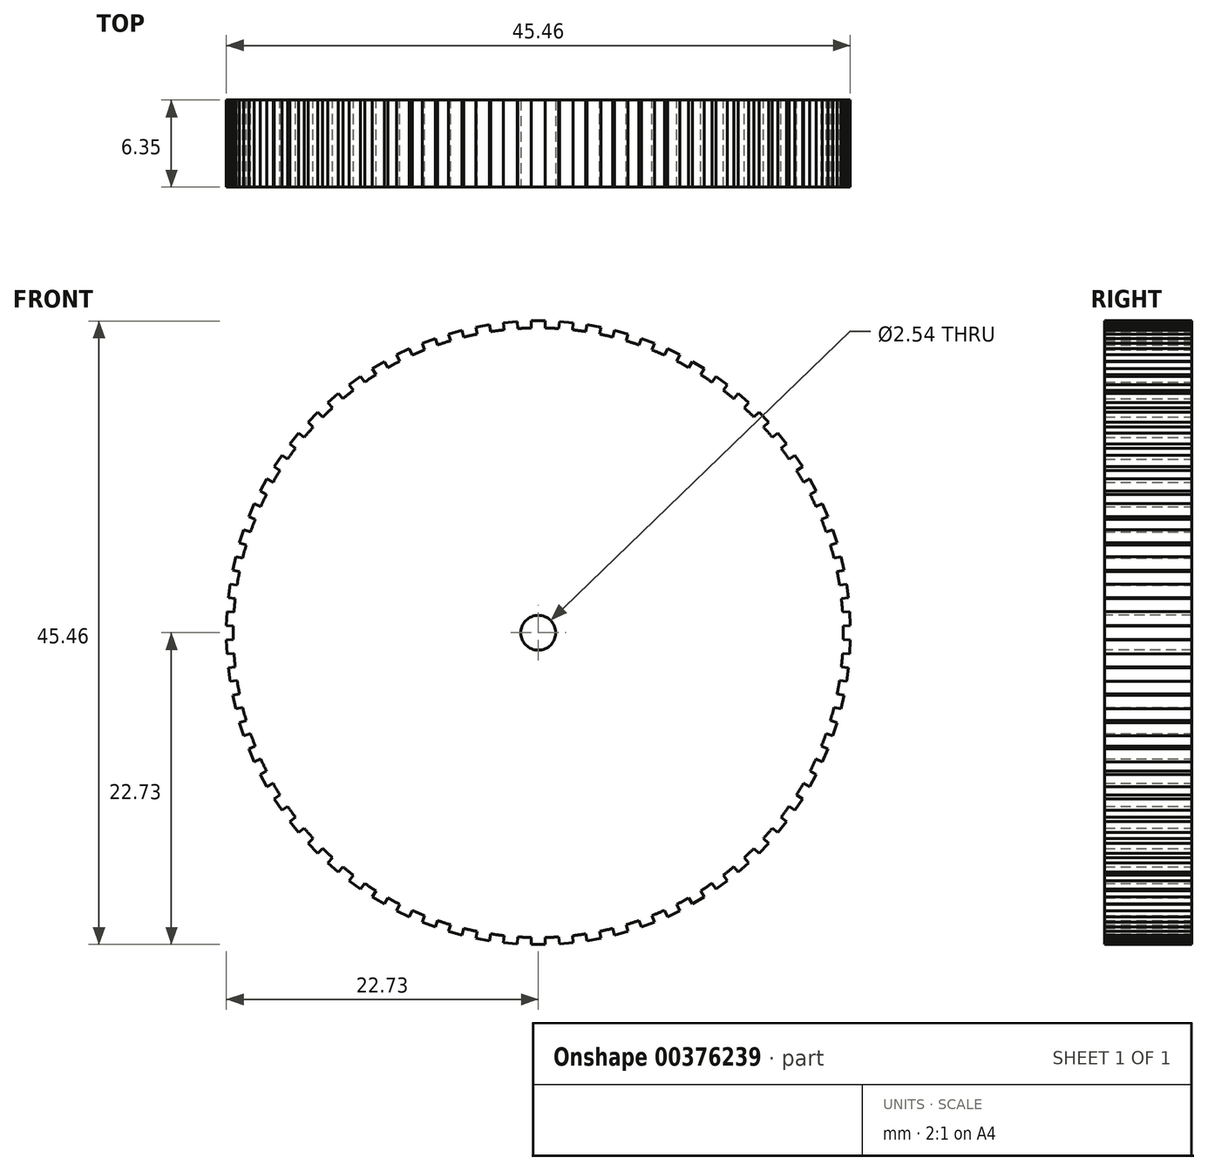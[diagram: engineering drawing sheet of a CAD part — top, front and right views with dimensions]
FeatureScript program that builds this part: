
annotation { "Feature Type Name" : "Feature", "Feature Type Description" : "" }
export const myFeature = defineFeature(function(context is Context, id is Id, definition is map)
    precondition{}
    {
        {
            var Q0;
            Q0=qCreatedBy(makeId("Front.planeOp"),FACE);
            var sketch = newSketch(context, id + "F0", { "sketchPlane" : qUnion([Q0])});
            skCircle(sketch, "E0", {"center": v(0, 0) * mm, "radius": 22.23 * mm});
            skLineSegment(sketch, "E1", {"start": v(0, 22.23) * mm, "end": v(0, 22.73) * mm});
            skLineSegment(sketch, "E2", {"start": v(0, 22.73) * mm, "end": v(0.5, 22.73) * mm});
            skLineSegment(sketch, "E3", {"start": v(0.5, 22.73) * mm, "end": v(0.5, 22.22) * mm});
            skLineSegment(sketch, "E4", {"start": v(0, 22.73) * mm, "end": v(-0.5, 22.73) * mm});
            skLineSegment(sketch, "E5", {"start": v(-0.5, 22.73) * mm, "end": v(-0.5, 22.22) * mm});
            skLineSegment(sketch, "E6.1.0", {"start": v(-1.53, 22.69) * mm, "end": v(-1.49, 22.18) * mm});
            skLineSegment(sketch, "E6.1.1", {"start": v(-2.04, 22.64) * mm, "end": v(-1.53, 22.69) * mm});
            skLineSegment(sketch, "E6.1.2", {"start": v(-2.04, 22.64) * mm, "end": v(-2.54, 22.6) * mm});
            skLineSegment(sketch, "E6.1.3", {"start": v(-2.54, 22.6) * mm, "end": v(-2.5, 22.08) * mm});
            skLineSegment(sketch, "E6.2.0", {"start": v(-3.56, 22.46) * mm, "end": v(-3.47, 21.95) * mm});
            skLineSegment(sketch, "E6.2.1", {"start": v(-4.06, 22.37) * mm, "end": v(-3.56, 22.46) * mm});
            skLineSegment(sketch, "E6.2.2", {"start": v(-4.06, 22.37) * mm, "end": v(-4.56, 22.28) * mm});
            skLineSegment(sketch, "E6.2.3", {"start": v(-4.56, 22.28) * mm, "end": v(-4.47, 21.77) * mm});
            skLineSegment(sketch, "E6.3.0", {"start": v(-5.56, 22.05) * mm, "end": v(-5.42, 21.55) * mm});
            skLineSegment(sketch, "E6.3.1", {"start": v(-6.05, 21.91) * mm, "end": v(-5.56, 22.05) * mm});
            skLineSegment(sketch, "E6.3.2", {"start": v(-6.05, 21.91) * mm, "end": v(-6.54, 21.78) * mm});
            skLineSegment(sketch, "E6.3.3", {"start": v(-6.54, 21.78) * mm, "end": v(-6.4, 21.28) * mm});
            skLineSegment(sketch, "E6.4.0", {"start": v(-7.51, 21.46) * mm, "end": v(-7.33, 20.98) * mm});
            skLineSegment(sketch, "E6.4.1", {"start": v(-7.99, 21.28) * mm, "end": v(-7.51, 21.46) * mm});
            skLineSegment(sketch, "E6.4.2", {"start": v(-7.99, 21.28) * mm, "end": v(-8.46, 21.1) * mm});
            skLineSegment(sketch, "E6.4.3", {"start": v(-8.46, 21.1) * mm, "end": v(-8.28, 20.62) * mm});
            skLineSegment(sketch, "E6.5.0", {"start": v(-9.4, 20.7) * mm, "end": v(-9.18, 20.24) * mm});
            skLineSegment(sketch, "E6.5.1", {"start": v(-9.86, 20.48) * mm, "end": v(-9.4, 20.7) * mm});
            skLineSegment(sketch, "E6.5.2", {"start": v(-9.86, 20.48) * mm, "end": v(-10.32, 20.26) * mm});
            skLineSegment(sketch, "E6.5.3", {"start": v(-10.32, 20.26) * mm, "end": v(-10.1, 19.8) * mm});
            skLineSegment(sketch, "E6.6.0", {"start": v(-11.22, 19.78) * mm, "end": v(-10.96, 19.33) * mm});
            skLineSegment(sketch, "E6.6.1", {"start": v(-11.66, 19.52) * mm, "end": v(-11.22, 19.78) * mm});
            skLineSegment(sketch, "E6.6.2", {"start": v(-11.66, 19.52) * mm, "end": v(-12.1, 19.25) * mm});
            skLineSegment(sketch, "E6.6.3", {"start": v(-12.1, 19.25) * mm, "end": v(-11.83, 18.81) * mm});
            skLineSegment(sketch, "E6.7.0", {"start": v(-12.95, 18.69) * mm, "end": v(-12.65, 18.27) * mm});
            skLineSegment(sketch, "E6.7.1", {"start": v(-13.36, 18.4) * mm, "end": v(-12.95, 18.69) * mm});
            skLineSegment(sketch, "E6.7.2", {"start": v(-13.36, 18.4) * mm, "end": v(-13.77, 18.1) * mm});
            skLineSegment(sketch, "E6.7.3", {"start": v(-13.77, 18.1) * mm, "end": v(-13.47, 17.68) * mm});
            skLineSegment(sketch, "E6.8.0", {"start": v(-14.57, 17.45) * mm, "end": v(-14.24, 17.07) * mm});
            skLineSegment(sketch, "E6.8.1", {"start": v(-14.96, 17.12) * mm, "end": v(-14.57, 17.45) * mm});
            skLineSegment(sketch, "E6.8.2", {"start": v(-14.96, 17.12) * mm, "end": v(-15.34, 16.79) * mm});
            skLineSegment(sketch, "E6.8.3", {"start": v(-15.34, 16.79) * mm, "end": v(-15, 16.4) * mm});
            skLineSegment(sketch, "E6.9.0", {"start": v(-16.08, 16.08) * mm, "end": v(-15.7, 15.72) * mm});
            skLineSegment(sketch, "E6.9.1", {"start": v(-16.43, 15.7) * mm, "end": v(-16.08, 16.08) * mm});
            skLineSegment(sketch, "E6.9.2", {"start": v(-16.43, 15.7) * mm, "end": v(-16.78, 15.34) * mm});
            skLineSegment(sketch, "E6.9.3", {"start": v(-16.78, 15.34) * mm, "end": v(-16.41, 14.99) * mm});
            skLineSegment(sketch, "E6.10.0", {"start": v(-17.46, 14.57) * mm, "end": v(-17.05, 14.25) * mm});
            skLineSegment(sketch, "E6.10.1", {"start": v(-17.77, 14.17) * mm, "end": v(-17.46, 14.57) * mm});
            skLineSegment(sketch, "E6.10.2", {"start": v(-17.77, 14.17) * mm, "end": v(-18.1, 13.78) * mm});
            skLineSegment(sketch, "E6.10.3", {"start": v(-18.1, 13.78) * mm, "end": v(-17.69, 13.46) * mm});
            skLineSegment(sketch, "E6.11.0", {"start": v(-18.7, 12.95) * mm, "end": v(-18.26, 12.66) * mm});
            skLineSegment(sketch, "E6.11.1", {"start": v(-18.97, 12.52) * mm, "end": v(-18.7, 12.95) * mm});
            skLineSegment(sketch, "E6.11.2", {"start": v(-18.97, 12.52) * mm, "end": v(-19.25, 12.1) * mm});
            skLineSegment(sketch, "E6.11.3", {"start": v(-19.25, 12.1) * mm, "end": v(-18.82, 11.82) * mm});
            skLineSegment(sketch, "E6.12.0", {"start": v(-19.78, 11.22) * mm, "end": v(-19.33, 10.98) * mm});
            skLineSegment(sketch, "E6.12.1", {"start": v(-20.02, 10.77) * mm, "end": v(-19.78, 11.22) * mm});
            skLineSegment(sketch, "E6.12.2", {"start": v(-20.02, 10.77) * mm, "end": v(-20.26, 10.33) * mm});
            skLineSegment(sketch, "E6.12.3", {"start": v(-20.26, 10.33) * mm, "end": v(-19.8, 10.08) * mm});
            skLineSegment(sketch, "E6.13.0", {"start": v(-20.7, 9.4) * mm, "end": v(-20.23, 9.2) * mm});
            skLineSegment(sketch, "E6.13.1", {"start": v(-20.9, 8.93) * mm, "end": v(-20.7, 9.4) * mm});
            skLineSegment(sketch, "E6.13.2", {"start": v(-20.9, 8.93) * mm, "end": v(-21.1, 8.47) * mm});
            skLineSegment(sketch, "E6.13.3", {"start": v(-21.1, 8.47) * mm, "end": v(-20.63, 8.27) * mm});
            skLineSegment(sketch, "E6.14.0", {"start": v(-21.46, 7.5) * mm, "end": v(-20.97, 7.35) * mm});
            skLineSegment(sketch, "E6.14.1", {"start": v(-21.62, 7.02) * mm, "end": v(-21.46, 7.5) * mm});
            skLineSegment(sketch, "E6.14.2", {"start": v(-21.62, 7.02) * mm, "end": v(-21.78, 6.54) * mm});
            skLineSegment(sketch, "E6.14.3", {"start": v(-21.78, 6.54) * mm, "end": v(-21.29, 6.38) * mm});
            skLineSegment(sketch, "E6.15.0", {"start": v(-22.05, 5.55) * mm, "end": v(-21.55, 5.44) * mm});
            skLineSegment(sketch, "E6.15.1", {"start": v(-22.16, 5.06) * mm, "end": v(-22.05, 5.55) * mm});
            skLineSegment(sketch, "E6.15.2", {"start": v(-22.16, 5.06) * mm, "end": v(-22.28, 4.56) * mm});
            skLineSegment(sketch, "E6.15.3", {"start": v(-22.28, 4.56) * mm, "end": v(-21.78, 4.45) * mm});
            skLineSegment(sketch, "E6.16.0", {"start": v(-22.46, 3.55) * mm, "end": v(-21.95, 3.49) * mm});
            skLineSegment(sketch, "E6.16.1", {"start": v(-22.53, 3.05) * mm, "end": v(-22.46, 3.55) * mm});
            skLineSegment(sketch, "E6.16.2", {"start": v(-22.53, 3.05) * mm, "end": v(-22.6, 2.55) * mm});
            skLineSegment(sketch, "E6.16.3", {"start": v(-22.6, 2.55) * mm, "end": v(-22.09, 2.48) * mm});
            skLineSegment(sketch, "E6.17.0", {"start": v(-22.69, 1.53) * mm, "end": v(-22.17, 1.5) * mm});
            skLineSegment(sketch, "E6.17.1", {"start": v(-22.71, 1.02) * mm, "end": v(-22.69, 1.53) * mm});
            skLineSegment(sketch, "E6.17.2", {"start": v(-22.71, 1.02) * mm, "end": v(-22.73, 0.51) * mm});
            skLineSegment(sketch, "E6.17.3", {"start": v(-22.73, 0.51) * mm, "end": v(-22.22, 0.49) * mm});
            skLineSegment(sketch, "E6.18.0", {"start": v(-22.73, -0.51) * mm, "end": v(-22.22, -0.49) * mm});
            skLineSegment(sketch, "E6.18.1", {"start": v(-22.71, -1.02) * mm, "end": v(-22.73, -0.51) * mm});
            skLineSegment(sketch, "E6.18.2", {"start": v(-22.71, -1.02) * mm, "end": v(-22.69, -1.53) * mm});
            skLineSegment(sketch, "E6.18.3", {"start": v(-22.69, -1.53) * mm, "end": v(-22.17, -1.5) * mm});
            skLineSegment(sketch, "E6.19.0", {"start": v(-22.6, -2.55) * mm, "end": v(-22.09, -2.48) * mm});
            skLineSegment(sketch, "E6.19.1", {"start": v(-22.53, -3.05) * mm, "end": v(-22.6, -2.55) * mm});
            skLineSegment(sketch, "E6.19.2", {"start": v(-22.53, -3.05) * mm, "end": v(-22.46, -3.55) * mm});
            skLineSegment(sketch, "E6.19.3", {"start": v(-22.46, -3.55) * mm, "end": v(-21.95, -3.49) * mm});
            skLineSegment(sketch, "E6.20.0", {"start": v(-22.28, -4.56) * mm, "end": v(-21.78, -4.45) * mm});
            skLineSegment(sketch, "E6.20.1", {"start": v(-22.16, -5.06) * mm, "end": v(-22.28, -4.56) * mm});
            skLineSegment(sketch, "E6.20.2", {"start": v(-22.16, -5.06) * mm, "end": v(-22.05, -5.55) * mm});
            skLineSegment(sketch, "E6.20.3", {"start": v(-22.05, -5.55) * mm, "end": v(-21.55, -5.44) * mm});
            skLineSegment(sketch, "E6.21.0", {"start": v(-21.78, -6.54) * mm, "end": v(-21.29, -6.38) * mm});
            skLineSegment(sketch, "E6.21.1", {"start": v(-21.62, -7.02) * mm, "end": v(-21.78, -6.54) * mm});
            skLineSegment(sketch, "E6.21.2", {"start": v(-21.62, -7.02) * mm, "end": v(-21.46, -7.5) * mm});
            skLineSegment(sketch, "E6.21.3", {"start": v(-21.46, -7.5) * mm, "end": v(-20.97, -7.35) * mm});
            skLineSegment(sketch, "E6.22.0", {"start": v(-21.1, -8.47) * mm, "end": v(-20.63, -8.27) * mm});
            skLineSegment(sketch, "E6.22.1", {"start": v(-20.9, -8.93) * mm, "end": v(-21.1, -8.47) * mm});
            skLineSegment(sketch, "E6.22.2", {"start": v(-20.9, -8.93) * mm, "end": v(-20.7, -9.4) * mm});
            skLineSegment(sketch, "E6.22.3", {"start": v(-20.7, -9.4) * mm, "end": v(-20.23, -9.2) * mm});
            skLineSegment(sketch, "E6.23.0", {"start": v(-20.26, -10.33) * mm, "end": v(-19.8, -10.08) * mm});
            skLineSegment(sketch, "E6.23.1", {"start": v(-20.02, -10.77) * mm, "end": v(-20.26, -10.33) * mm});
            skLineSegment(sketch, "E6.23.2", {"start": v(-20.02, -10.77) * mm, "end": v(-19.78, -11.22) * mm});
            skLineSegment(sketch, "E6.23.3", {"start": v(-19.78, -11.22) * mm, "end": v(-19.33, -10.98) * mm});
            skLineSegment(sketch, "E6.24.0", {"start": v(-19.25, -12.1) * mm, "end": v(-18.82, -11.82) * mm});
            skLineSegment(sketch, "E6.24.1", {"start": v(-18.97, -12.52) * mm, "end": v(-19.25, -12.1) * mm});
            skLineSegment(sketch, "E6.24.2", {"start": v(-18.97, -12.52) * mm, "end": v(-18.7, -12.95) * mm});
            skLineSegment(sketch, "E6.24.3", {"start": v(-18.7, -12.95) * mm, "end": v(-18.26, -12.66) * mm});
            skLineSegment(sketch, "E6.25.0", {"start": v(-18.1, -13.78) * mm, "end": v(-17.69, -13.46) * mm});
            skLineSegment(sketch, "E6.25.1", {"start": v(-17.77, -14.17) * mm, "end": v(-18.1, -13.78) * mm});
            skLineSegment(sketch, "E6.25.2", {"start": v(-17.77, -14.17) * mm, "end": v(-17.46, -14.57) * mm});
            skLineSegment(sketch, "E6.25.3", {"start": v(-17.46, -14.57) * mm, "end": v(-17.05, -14.25) * mm});
            skLineSegment(sketch, "E6.26.0", {"start": v(-16.78, -15.34) * mm, "end": v(-16.41, -14.99) * mm});
            skLineSegment(sketch, "E6.26.1", {"start": v(-16.43, -15.7) * mm, "end": v(-16.78, -15.34) * mm});
            skLineSegment(sketch, "E6.26.2", {"start": v(-16.43, -15.7) * mm, "end": v(-16.08, -16.08) * mm});
            skLineSegment(sketch, "E6.26.3", {"start": v(-16.08, -16.08) * mm, "end": v(-15.7, -15.72) * mm});
            skLineSegment(sketch, "E6.27.0", {"start": v(-15.34, -16.79) * mm, "end": v(-15, -16.4) * mm});
            skLineSegment(sketch, "E6.27.1", {"start": v(-14.96, -17.12) * mm, "end": v(-15.34, -16.79) * mm});
            skLineSegment(sketch, "E6.27.2", {"start": v(-14.96, -17.12) * mm, "end": v(-14.57, -17.45) * mm});
            skLineSegment(sketch, "E6.27.3", {"start": v(-14.57, -17.45) * mm, "end": v(-14.24, -17.07) * mm});
            skLineSegment(sketch, "E6.28.0", {"start": v(-13.77, -18.1) * mm, "end": v(-13.47, -17.68) * mm});
            skLineSegment(sketch, "E6.28.1", {"start": v(-13.36, -18.4) * mm, "end": v(-13.77, -18.1) * mm});
            skLineSegment(sketch, "E6.28.2", {"start": v(-13.36, -18.4) * mm, "end": v(-12.95, -18.69) * mm});
            skLineSegment(sketch, "E6.28.3", {"start": v(-12.95, -18.69) * mm, "end": v(-12.65, -18.27) * mm});
            skLineSegment(sketch, "E6.29.0", {"start": v(-12.1, -19.25) * mm, "end": v(-11.83, -18.81) * mm});
            skLineSegment(sketch, "E6.29.1", {"start": v(-11.66, -19.52) * mm, "end": v(-12.1, -19.25) * mm});
            skLineSegment(sketch, "E6.29.2", {"start": v(-11.66, -19.52) * mm, "end": v(-11.22, -19.78) * mm});
            skLineSegment(sketch, "E6.29.3", {"start": v(-11.22, -19.78) * mm, "end": v(-10.96, -19.33) * mm});
            skLineSegment(sketch, "E6.30.0", {"start": v(-10.32, -20.26) * mm, "end": v(-10.1, -19.8) * mm});
            skLineSegment(sketch, "E6.30.1", {"start": v(-9.86, -20.48) * mm, "end": v(-10.32, -20.26) * mm});
            skLineSegment(sketch, "E6.30.2", {"start": v(-9.86, -20.48) * mm, "end": v(-9.4, -20.7) * mm});
            skLineSegment(sketch, "E6.30.3", {"start": v(-9.4, -20.7) * mm, "end": v(-9.18, -20.24) * mm});
            skLineSegment(sketch, "E6.31.0", {"start": v(-8.46, -21.1) * mm, "end": v(-8.28, -20.62) * mm});
            skLineSegment(sketch, "E6.31.1", {"start": v(-7.99, -21.28) * mm, "end": v(-8.46, -21.1) * mm});
            skLineSegment(sketch, "E6.31.2", {"start": v(-7.99, -21.28) * mm, "end": v(-7.51, -21.46) * mm});
            skLineSegment(sketch, "E6.31.3", {"start": v(-7.51, -21.46) * mm, "end": v(-7.33, -20.98) * mm});
            skLineSegment(sketch, "E6.32.0", {"start": v(-6.54, -21.78) * mm, "end": v(-6.4, -21.28) * mm});
            skLineSegment(sketch, "E6.32.1", {"start": v(-6.05, -21.91) * mm, "end": v(-6.54, -21.78) * mm});
            skLineSegment(sketch, "E6.32.2", {"start": v(-6.05, -21.91) * mm, "end": v(-5.56, -22.05) * mm});
            skLineSegment(sketch, "E6.32.3", {"start": v(-5.56, -22.05) * mm, "end": v(-5.42, -21.55) * mm});
            skLineSegment(sketch, "E6.33.0", {"start": v(-4.56, -22.28) * mm, "end": v(-4.47, -21.77) * mm});
            skLineSegment(sketch, "E6.33.1", {"start": v(-4.06, -22.37) * mm, "end": v(-4.56, -22.28) * mm});
            skLineSegment(sketch, "E6.33.2", {"start": v(-4.06, -22.37) * mm, "end": v(-3.56, -22.46) * mm});
            skLineSegment(sketch, "E6.33.3", {"start": v(-3.56, -22.46) * mm, "end": v(-3.47, -21.95) * mm});
            skLineSegment(sketch, "E6.34.0", {"start": v(-2.54, -22.6) * mm, "end": v(-2.5, -22.08) * mm});
            skLineSegment(sketch, "E6.34.1", {"start": v(-2.04, -22.64) * mm, "end": v(-2.54, -22.6) * mm});
            skLineSegment(sketch, "E6.34.2", {"start": v(-2.04, -22.64) * mm, "end": v(-1.53, -22.69) * mm});
            skLineSegment(sketch, "E6.34.3", {"start": v(-1.53, -22.69) * mm, "end": v(-1.49, -22.18) * mm});
            skLineSegment(sketch, "E6.35.0", {"start": v(-0.5, -22.73) * mm, "end": v(-0.5, -22.22) * mm});
            skLineSegment(sketch, "E6.35.1", {"start": v(0, -22.73) * mm, "end": v(-0.5, -22.73) * mm});
            skLineSegment(sketch, "E6.35.2", {"start": v(0, -22.73) * mm, "end": v(0.5, -22.73) * mm});
            skLineSegment(sketch, "E6.35.3", {"start": v(0.5, -22.73) * mm, "end": v(0.5, -22.22) * mm});
            skLineSegment(sketch, "E6.36.0", {"start": v(1.53, -22.69) * mm, "end": v(1.49, -22.18) * mm});
            skLineSegment(sketch, "E6.36.1", {"start": v(2.04, -22.64) * mm, "end": v(1.53, -22.69) * mm});
            skLineSegment(sketch, "E6.36.2", {"start": v(2.04, -22.64) * mm, "end": v(2.54, -22.6) * mm});
            skLineSegment(sketch, "E6.36.3", {"start": v(2.54, -22.6) * mm, "end": v(2.5, -22.08) * mm});
            skLineSegment(sketch, "E6.37.0", {"start": v(3.56, -22.46) * mm, "end": v(3.47, -21.95) * mm});
            skLineSegment(sketch, "E6.37.1", {"start": v(4.06, -22.37) * mm, "end": v(3.56, -22.46) * mm});
            skLineSegment(sketch, "E6.37.2", {"start": v(4.06, -22.37) * mm, "end": v(4.56, -22.28) * mm});
            skLineSegment(sketch, "E6.37.3", {"start": v(4.56, -22.28) * mm, "end": v(4.47, -21.77) * mm});
            skLineSegment(sketch, "E6.38.0", {"start": v(5.56, -22.05) * mm, "end": v(5.42, -21.55) * mm});
            skLineSegment(sketch, "E6.38.1", {"start": v(6.05, -21.91) * mm, "end": v(5.56, -22.05) * mm});
            skLineSegment(sketch, "E6.38.2", {"start": v(6.05, -21.91) * mm, "end": v(6.54, -21.78) * mm});
            skLineSegment(sketch, "E6.38.3", {"start": v(6.54, -21.78) * mm, "end": v(6.4, -21.28) * mm});
            skLineSegment(sketch, "E6.39.0", {"start": v(7.51, -21.46) * mm, "end": v(7.33, -20.98) * mm});
            skLineSegment(sketch, "E6.39.1", {"start": v(7.99, -21.28) * mm, "end": v(7.51, -21.46) * mm});
            skLineSegment(sketch, "E6.39.2", {"start": v(7.99, -21.28) * mm, "end": v(8.46, -21.1) * mm});
            skLineSegment(sketch, "E6.39.3", {"start": v(8.46, -21.1) * mm, "end": v(8.28, -20.62) * mm});
            skLineSegment(sketch, "E6.40.0", {"start": v(9.4, -20.7) * mm, "end": v(9.18, -20.24) * mm});
            skLineSegment(sketch, "E6.40.1", {"start": v(9.86, -20.48) * mm, "end": v(9.4, -20.7) * mm});
            skLineSegment(sketch, "E6.40.2", {"start": v(9.86, -20.48) * mm, "end": v(10.32, -20.26) * mm});
            skLineSegment(sketch, "E6.40.3", {"start": v(10.32, -20.26) * mm, "end": v(10.1, -19.8) * mm});
            skLineSegment(sketch, "E6.41.0", {"start": v(11.22, -19.78) * mm, "end": v(10.96, -19.33) * mm});
            skLineSegment(sketch, "E6.41.1", {"start": v(11.66, -19.52) * mm, "end": v(11.22, -19.78) * mm});
            skLineSegment(sketch, "E6.41.2", {"start": v(11.66, -19.52) * mm, "end": v(12.1, -19.25) * mm});
            skLineSegment(sketch, "E6.41.3", {"start": v(12.1, -19.25) * mm, "end": v(11.83, -18.81) * mm});
            skLineSegment(sketch, "E6.42.0", {"start": v(12.95, -18.69) * mm, "end": v(12.65, -18.27) * mm});
            skLineSegment(sketch, "E6.42.1", {"start": v(13.36, -18.4) * mm, "end": v(12.95, -18.69) * mm});
            skLineSegment(sketch, "E6.42.2", {"start": v(13.36, -18.4) * mm, "end": v(13.77, -18.1) * mm});
            skLineSegment(sketch, "E6.42.3", {"start": v(13.77, -18.1) * mm, "end": v(13.47, -17.68) * mm});
            skLineSegment(sketch, "E6.43.0", {"start": v(14.57, -17.45) * mm, "end": v(14.24, -17.07) * mm});
            skLineSegment(sketch, "E6.43.1", {"start": v(14.96, -17.12) * mm, "end": v(14.57, -17.45) * mm});
            skLineSegment(sketch, "E6.43.2", {"start": v(14.96, -17.12) * mm, "end": v(15.34, -16.79) * mm});
            skLineSegment(sketch, "E6.43.3", {"start": v(15.34, -16.79) * mm, "end": v(15, -16.4) * mm});
            skLineSegment(sketch, "E6.44.0", {"start": v(16.08, -16.08) * mm, "end": v(15.7, -15.72) * mm});
            skLineSegment(sketch, "E6.44.1", {"start": v(16.43, -15.7) * mm, "end": v(16.08, -16.08) * mm});
            skLineSegment(sketch, "E6.44.2", {"start": v(16.43, -15.7) * mm, "end": v(16.78, -15.34) * mm});
            skLineSegment(sketch, "E6.44.3", {"start": v(16.78, -15.34) * mm, "end": v(16.41, -14.99) * mm});
            skLineSegment(sketch, "E6.45.0", {"start": v(17.46, -14.57) * mm, "end": v(17.05, -14.25) * mm});
            skLineSegment(sketch, "E6.45.1", {"start": v(17.77, -14.17) * mm, "end": v(17.46, -14.57) * mm});
            skLineSegment(sketch, "E6.45.2", {"start": v(17.77, -14.17) * mm, "end": v(18.1, -13.78) * mm});
            skLineSegment(sketch, "E6.45.3", {"start": v(18.1, -13.78) * mm, "end": v(17.69, -13.46) * mm});
            skLineSegment(sketch, "E6.46.0", {"start": v(18.7, -12.95) * mm, "end": v(18.26, -12.66) * mm});
            skLineSegment(sketch, "E6.46.1", {"start": v(18.97, -12.52) * mm, "end": v(18.7, -12.95) * mm});
            skLineSegment(sketch, "E6.46.2", {"start": v(18.97, -12.52) * mm, "end": v(19.25, -12.1) * mm});
            skLineSegment(sketch, "E6.46.3", {"start": v(19.25, -12.1) * mm, "end": v(18.82, -11.82) * mm});
            skLineSegment(sketch, "E6.47.0", {"start": v(19.78, -11.22) * mm, "end": v(19.33, -10.98) * mm});
            skLineSegment(sketch, "E6.47.1", {"start": v(20.02, -10.77) * mm, "end": v(19.78, -11.22) * mm});
            skLineSegment(sketch, "E6.47.2", {"start": v(20.02, -10.77) * mm, "end": v(20.26, -10.33) * mm});
            skLineSegment(sketch, "E6.47.3", {"start": v(20.26, -10.33) * mm, "end": v(19.8, -10.08) * mm});
            skLineSegment(sketch, "E6.48.0", {"start": v(20.7, -9.4) * mm, "end": v(20.23, -9.2) * mm});
            skLineSegment(sketch, "E6.48.1", {"start": v(20.9, -8.93) * mm, "end": v(20.7, -9.4) * mm});
            skLineSegment(sketch, "E6.48.2", {"start": v(20.9, -8.93) * mm, "end": v(21.1, -8.47) * mm});
            skLineSegment(sketch, "E6.48.3", {"start": v(21.1, -8.47) * mm, "end": v(20.63, -8.27) * mm});
            skLineSegment(sketch, "E6.49.0", {"start": v(21.46, -7.5) * mm, "end": v(20.97, -7.35) * mm});
            skLineSegment(sketch, "E6.49.1", {"start": v(21.62, -7.02) * mm, "end": v(21.46, -7.5) * mm});
            skLineSegment(sketch, "E6.49.2", {"start": v(21.62, -7.02) * mm, "end": v(21.78, -6.54) * mm});
            skLineSegment(sketch, "E6.49.3", {"start": v(21.78, -6.54) * mm, "end": v(21.29, -6.38) * mm});
            skLineSegment(sketch, "E6.50.0", {"start": v(22.05, -5.55) * mm, "end": v(21.55, -5.44) * mm});
            skLineSegment(sketch, "E6.50.1", {"start": v(22.16, -5.06) * mm, "end": v(22.05, -5.55) * mm});
            skLineSegment(sketch, "E6.50.2", {"start": v(22.16, -5.06) * mm, "end": v(22.28, -4.56) * mm});
            skLineSegment(sketch, "E6.50.3", {"start": v(22.28, -4.56) * mm, "end": v(21.78, -4.45) * mm});
            skLineSegment(sketch, "E6.51.0", {"start": v(22.46, -3.55) * mm, "end": v(21.95, -3.49) * mm});
            skLineSegment(sketch, "E6.51.1", {"start": v(22.53, -3.05) * mm, "end": v(22.46, -3.55) * mm});
            skLineSegment(sketch, "E6.51.2", {"start": v(22.53, -3.05) * mm, "end": v(22.6, -2.55) * mm});
            skLineSegment(sketch, "E6.51.3", {"start": v(22.6, -2.55) * mm, "end": v(22.09, -2.48) * mm});
            skLineSegment(sketch, "E6.52.0", {"start": v(22.69, -1.53) * mm, "end": v(22.17, -1.5) * mm});
            skLineSegment(sketch, "E6.52.1", {"start": v(22.71, -1.02) * mm, "end": v(22.69, -1.53) * mm});
            skLineSegment(sketch, "E6.52.2", {"start": v(22.71, -1.02) * mm, "end": v(22.73, -0.51) * mm});
            skLineSegment(sketch, "E6.52.3", {"start": v(22.73, -0.51) * mm, "end": v(22.22, -0.49) * mm});
            skLineSegment(sketch, "E6.53.0", {"start": v(22.73, 0.51) * mm, "end": v(22.22, 0.49) * mm});
            skLineSegment(sketch, "E6.53.1", {"start": v(22.71, 1.02) * mm, "end": v(22.73, 0.51) * mm});
            skLineSegment(sketch, "E6.53.2", {"start": v(22.71, 1.02) * mm, "end": v(22.69, 1.53) * mm});
            skLineSegment(sketch, "E6.53.3", {"start": v(22.69, 1.53) * mm, "end": v(22.17, 1.5) * mm});
            skLineSegment(sketch, "E6.54.0", {"start": v(22.6, 2.55) * mm, "end": v(22.09, 2.48) * mm});
            skLineSegment(sketch, "E6.54.1", {"start": v(22.53, 3.05) * mm, "end": v(22.6, 2.55) * mm});
            skLineSegment(sketch, "E6.54.2", {"start": v(22.53, 3.05) * mm, "end": v(22.46, 3.55) * mm});
            skLineSegment(sketch, "E6.54.3", {"start": v(22.46, 3.55) * mm, "end": v(21.95, 3.49) * mm});
            skLineSegment(sketch, "E6.55.0", {"start": v(22.28, 4.56) * mm, "end": v(21.78, 4.45) * mm});
            skLineSegment(sketch, "E6.55.1", {"start": v(22.16, 5.06) * mm, "end": v(22.28, 4.56) * mm});
            skLineSegment(sketch, "E6.55.2", {"start": v(22.16, 5.06) * mm, "end": v(22.05, 5.55) * mm});
            skLineSegment(sketch, "E6.55.3", {"start": v(22.05, 5.55) * mm, "end": v(21.55, 5.44) * mm});
            skLineSegment(sketch, "E6.56.0", {"start": v(21.78, 6.54) * mm, "end": v(21.29, 6.38) * mm});
            skLineSegment(sketch, "E6.56.1", {"start": v(21.62, 7.02) * mm, "end": v(21.78, 6.54) * mm});
            skLineSegment(sketch, "E6.56.2", {"start": v(21.62, 7.02) * mm, "end": v(21.46, 7.5) * mm});
            skLineSegment(sketch, "E6.56.3", {"start": v(21.46, 7.5) * mm, "end": v(20.97, 7.35) * mm});
            skLineSegment(sketch, "E6.57.0", {"start": v(21.1, 8.47) * mm, "end": v(20.63, 8.27) * mm});
            skLineSegment(sketch, "E6.57.1", {"start": v(20.9, 8.93) * mm, "end": v(21.1, 8.47) * mm});
            skLineSegment(sketch, "E6.57.2", {"start": v(20.9, 8.93) * mm, "end": v(20.7, 9.4) * mm});
            skLineSegment(sketch, "E6.57.3", {"start": v(20.7, 9.4) * mm, "end": v(20.23, 9.2) * mm});
            skLineSegment(sketch, "E6.58.0", {"start": v(20.26, 10.33) * mm, "end": v(19.8, 10.08) * mm});
            skLineSegment(sketch, "E6.58.1", {"start": v(20.02, 10.77) * mm, "end": v(20.26, 10.33) * mm});
            skLineSegment(sketch, "E6.58.2", {"start": v(20.02, 10.77) * mm, "end": v(19.78, 11.22) * mm});
            skLineSegment(sketch, "E6.58.3", {"start": v(19.78, 11.22) * mm, "end": v(19.33, 10.98) * mm});
            skLineSegment(sketch, "E6.59.0", {"start": v(19.25, 12.1) * mm, "end": v(18.82, 11.82) * mm});
            skLineSegment(sketch, "E6.59.1", {"start": v(18.97, 12.52) * mm, "end": v(19.25, 12.1) * mm});
            skLineSegment(sketch, "E6.59.2", {"start": v(18.97, 12.52) * mm, "end": v(18.7, 12.95) * mm});
            skLineSegment(sketch, "E6.59.3", {"start": v(18.7, 12.95) * mm, "end": v(18.26, 12.66) * mm});
            skLineSegment(sketch, "E6.60.0", {"start": v(18.1, 13.78) * mm, "end": v(17.69, 13.46) * mm});
            skLineSegment(sketch, "E6.60.1", {"start": v(17.77, 14.17) * mm, "end": v(18.1, 13.78) * mm});
            skLineSegment(sketch, "E6.60.2", {"start": v(17.77, 14.17) * mm, "end": v(17.46, 14.57) * mm});
            skLineSegment(sketch, "E6.60.3", {"start": v(17.46, 14.57) * mm, "end": v(17.05, 14.25) * mm});
            skLineSegment(sketch, "E6.61.0", {"start": v(16.78, 15.34) * mm, "end": v(16.41, 14.99) * mm});
            skLineSegment(sketch, "E6.61.1", {"start": v(16.43, 15.7) * mm, "end": v(16.78, 15.34) * mm});
            skLineSegment(sketch, "E6.61.2", {"start": v(16.43, 15.7) * mm, "end": v(16.08, 16.08) * mm});
            skLineSegment(sketch, "E6.61.3", {"start": v(16.08, 16.08) * mm, "end": v(15.7, 15.72) * mm});
            skLineSegment(sketch, "E6.62.0", {"start": v(15.34, 16.79) * mm, "end": v(15, 16.4) * mm});
            skLineSegment(sketch, "E6.62.1", {"start": v(14.96, 17.12) * mm, "end": v(15.34, 16.79) * mm});
            skLineSegment(sketch, "E6.62.2", {"start": v(14.96, 17.12) * mm, "end": v(14.57, 17.45) * mm});
            skLineSegment(sketch, "E6.62.3", {"start": v(14.57, 17.45) * mm, "end": v(14.24, 17.07) * mm});
            skLineSegment(sketch, "E6.63.0", {"start": v(13.77, 18.1) * mm, "end": v(13.47, 17.68) * mm});
            skLineSegment(sketch, "E6.63.1", {"start": v(13.36, 18.4) * mm, "end": v(13.77, 18.1) * mm});
            skLineSegment(sketch, "E6.63.2", {"start": v(13.36, 18.4) * mm, "end": v(12.95, 18.69) * mm});
            skLineSegment(sketch, "E6.63.3", {"start": v(12.95, 18.69) * mm, "end": v(12.65, 18.27) * mm});
            skLineSegment(sketch, "E6.64.0", {"start": v(12.1, 19.25) * mm, "end": v(11.83, 18.81) * mm});
            skLineSegment(sketch, "E6.64.1", {"start": v(11.66, 19.52) * mm, "end": v(12.1, 19.25) * mm});
            skLineSegment(sketch, "E6.64.2", {"start": v(11.66, 19.52) * mm, "end": v(11.22, 19.78) * mm});
            skLineSegment(sketch, "E6.64.3", {"start": v(11.22, 19.78) * mm, "end": v(10.96, 19.33) * mm});
            skLineSegment(sketch, "E6.65.0", {"start": v(10.32, 20.26) * mm, "end": v(10.1, 19.8) * mm});
            skLineSegment(sketch, "E6.65.1", {"start": v(9.86, 20.48) * mm, "end": v(10.32, 20.26) * mm});
            skLineSegment(sketch, "E6.65.2", {"start": v(9.86, 20.48) * mm, "end": v(9.4, 20.7) * mm});
            skLineSegment(sketch, "E6.65.3", {"start": v(9.4, 20.7) * mm, "end": v(9.18, 20.24) * mm});
            skLineSegment(sketch, "E6.66.0", {"start": v(8.46, 21.1) * mm, "end": v(8.28, 20.62) * mm});
            skLineSegment(sketch, "E6.66.1", {"start": v(7.99, 21.28) * mm, "end": v(8.46, 21.1) * mm});
            skLineSegment(sketch, "E6.66.2", {"start": v(7.99, 21.28) * mm, "end": v(7.51, 21.46) * mm});
            skLineSegment(sketch, "E6.66.3", {"start": v(7.51, 21.46) * mm, "end": v(7.33, 20.98) * mm});
            skLineSegment(sketch, "E6.67.0", {"start": v(6.54, 21.78) * mm, "end": v(6.4, 21.28) * mm});
            skLineSegment(sketch, "E6.67.1", {"start": v(6.05, 21.91) * mm, "end": v(6.54, 21.78) * mm});
            skLineSegment(sketch, "E6.67.2", {"start": v(6.05, 21.91) * mm, "end": v(5.56, 22.05) * mm});
            skLineSegment(sketch, "E6.67.3", {"start": v(5.56, 22.05) * mm, "end": v(5.42, 21.55) * mm});
            skLineSegment(sketch, "E6.68.0", {"start": v(4.56, 22.28) * mm, "end": v(4.47, 21.77) * mm});
            skLineSegment(sketch, "E6.68.1", {"start": v(4.06, 22.37) * mm, "end": v(4.56, 22.28) * mm});
            skLineSegment(sketch, "E6.68.2", {"start": v(4.06, 22.37) * mm, "end": v(3.56, 22.46) * mm});
            skLineSegment(sketch, "E6.68.3", {"start": v(3.56, 22.46) * mm, "end": v(3.47, 21.95) * mm});
            skLineSegment(sketch, "E6.69.0", {"start": v(2.54, 22.6) * mm, "end": v(2.5, 22.08) * mm});
            skLineSegment(sketch, "E6.69.1", {"start": v(2.04, 22.64) * mm, "end": v(2.54, 22.6) * mm});
            skLineSegment(sketch, "E6.69.2", {"start": v(2.04, 22.64) * mm, "end": v(1.53, 22.69) * mm});
            skLineSegment(sketch, "E6.69.3", {"start": v(1.53, 22.69) * mm, "end": v(1.49, 22.18) * mm});
            skSolve(sketch);
        }
        {
            var Q0;
            {var subQ0=sQuery(id+"F0.wireOp",EDGE,"E6.16.0");Q0=makeQuery(id+"F0.imprint","IMPRINT",FACE,{"disambiguationData":[TD([[makeQuery(id+"F0.imprint","IMPRINT",EDGE,{"derivedFrom":subQ0}),-1.0]])]});}
            var Q1;
            {var subQ0=sQuery(id+"F0.wireOp",EDGE,"E6.29.0");Q1=makeQuery(id+"F0.imprint","IMPRINT",FACE,{"disambiguationData":[TD([[makeQuery(id+"F0.imprint","IMPRINT",EDGE,{"derivedFrom":subQ0}),-1.0]])]});}
            var Q2;
            {var subQ0=sQuery(id+"F0.wireOp",EDGE,"E6.13.0");Q2=makeQuery(id+"F0.imprint","IMPRINT",FACE,{"disambiguationData":[TD([[makeQuery(id+"F0.imprint","IMPRINT",EDGE,{"derivedFrom":subQ0}),-1.0]])]});}
            var Q3;
            {var subQ0=sQuery(id+"F0.wireOp",EDGE,"E6.14.0");Q3=makeQuery(id+"F0.imprint","IMPRINT",FACE,{"disambiguationData":[TD([[makeQuery(id+"F0.imprint","IMPRINT",EDGE,{"derivedFrom":subQ0}),-1.0]])]});}
            var Q4;
            {var subQ0=sQuery(id+"F0.wireOp",EDGE,"E6.46.0");Q4=makeQuery(id+"F0.imprint","IMPRINT",FACE,{"disambiguationData":[TD([[makeQuery(id+"F0.imprint","IMPRINT",EDGE,{"derivedFrom":subQ0}),-1.0]])]});}
            var Q5;
            {var subQ0=sQuery(id+"F0.wireOp",EDGE,"E6.30.0");Q5=makeQuery(id+"F0.imprint","IMPRINT",FACE,{"disambiguationData":[TD([[makeQuery(id+"F0.imprint","IMPRINT",EDGE,{"derivedFrom":subQ0}),-1.0]])]});}
            var Q6;
            {var subQ0=sQuery(id+"F0.wireOp",EDGE,"E6.47.0");Q6=makeQuery(id+"F0.imprint","IMPRINT",FACE,{"disambiguationData":[TD([[makeQuery(id+"F0.imprint","IMPRINT",EDGE,{"derivedFrom":subQ0}),-1.0]])]});}
            var Q7;
            {var subQ0=sQuery(id+"F0.wireOp",EDGE,"E6.15.0");Q7=makeQuery(id+"F0.imprint","IMPRINT",FACE,{"disambiguationData":[TD([[makeQuery(id+"F0.imprint","IMPRINT",EDGE,{"derivedFrom":subQ0}),-1.0]])]});}
            var Q8;
            {var subQ0=sQuery(id+"F0.wireOp",EDGE,"E6.50.0");Q8=makeQuery(id+"F0.imprint","IMPRINT",FACE,{"disambiguationData":[TD([[makeQuery(id+"F0.imprint","IMPRINT",EDGE,{"derivedFrom":subQ0}),-1.0]])]});}
            var Q9;
            {var subQ0=sQuery(id+"F0.wireOp",EDGE,"E6.18.0");Q9=makeQuery(id+"F0.imprint","IMPRINT",FACE,{"disambiguationData":[TD([[makeQuery(id+"F0.imprint","IMPRINT",EDGE,{"derivedFrom":subQ0}),-1.0]])]});}
            var Q10;
            {var subQ0=sQuery(id+"F0.wireOp",EDGE,"E6.20.0");Q10=makeQuery(id+"F0.imprint","IMPRINT",FACE,{"disambiguationData":[TD([[makeQuery(id+"F0.imprint","IMPRINT",EDGE,{"derivedFrom":subQ0}),-1.0]])]});}
            var Q11;
            {var subQ0=sQuery(id+"F0.wireOp",EDGE,"E6.4.0");Q11=makeQuery(id+"F0.imprint","IMPRINT",FACE,{"disambiguationData":[TD([[makeQuery(id+"F0.imprint","IMPRINT",EDGE,{"derivedFrom":subQ0}),-1.0]])]});}
            var Q12;
            {var subQ0=sQuery(id+"F0.wireOp",EDGE,"E6.6.0");Q12=makeQuery(id+"F0.imprint","IMPRINT",FACE,{"disambiguationData":[TD([[makeQuery(id+"F0.imprint","IMPRINT",EDGE,{"derivedFrom":subQ0}),-1.0]])]});}
            var Q13;
            {var subQ0=sQuery(id+"F0.wireOp",EDGE,"E6.21.0");Q13=makeQuery(id+"F0.imprint","IMPRINT",FACE,{"disambiguationData":[TD([[makeQuery(id+"F0.imprint","IMPRINT",EDGE,{"derivedFrom":subQ0}),-1.0]])]});}
            var Q14;
            {var subQ0=sQuery(id+"F0.wireOp",EDGE,"E6.5.0");Q14=makeQuery(id+"F0.imprint","IMPRINT",FACE,{"disambiguationData":[TD([[makeQuery(id+"F0.imprint","IMPRINT",EDGE,{"derivedFrom":subQ0}),-1.0]])]});}
            var Q15;
            {var subQ0=sQuery(id+"F0.wireOp",EDGE,"E6.22.0");Q15=makeQuery(id+"F0.imprint","IMPRINT",FACE,{"disambiguationData":[TD([[makeQuery(id+"F0.imprint","IMPRINT",EDGE,{"derivedFrom":subQ0}),-1.0]])]});}
            var Q16;
            {var subQ0=sQuery(id+"F0.wireOp",EDGE,"E6.9.0");Q16=makeQuery(id+"F0.imprint","IMPRINT",FACE,{"disambiguationData":[TD([[makeQuery(id+"F0.imprint","IMPRINT",EDGE,{"derivedFrom":subQ0}),-1.0]])]});}
            var Q17;
            {var subQ0=sQuery(id+"F0.wireOp",EDGE,"E6.25.0");Q17=makeQuery(id+"F0.imprint","IMPRINT",FACE,{"disambiguationData":[TD([[makeQuery(id+"F0.imprint","IMPRINT",EDGE,{"derivedFrom":subQ0}),-1.0]])]});}
            var Q18;
            {var subQ0=sQuery(id+"F0.wireOp",EDGE,"E6.41.0");Q18=makeQuery(id+"F0.imprint","IMPRINT",FACE,{"disambiguationData":[TD([[makeQuery(id+"F0.imprint","IMPRINT",EDGE,{"derivedFrom":subQ0}),-1.0]])]});}
            var Q19;
            {var subQ0=sQuery(id+"F0.wireOp",EDGE,"E6.56.0");Q19=makeQuery(id+"F0.imprint","IMPRINT",FACE,{"disambiguationData":[TD([[makeQuery(id+"F0.imprint","IMPRINT",EDGE,{"derivedFrom":subQ0}),-1.0]])]});}
            var Q20;
            {var subQ0=sQuery(id+"F0.wireOp",EDGE,"E6.65.0");Q20=makeQuery(id+"F0.imprint","IMPRINT",FACE,{"disambiguationData":[TD([[makeQuery(id+"F0.imprint","IMPRINT",EDGE,{"derivedFrom":subQ0}),-1.0]])]});}
            var Q21;
            {var subQ0=sQuery(id+"F0.wireOp",EDGE,"E6.61.0");Q21=makeQuery(id+"F0.imprint","IMPRINT",FACE,{"disambiguationData":[TD([[makeQuery(id+"F0.imprint","IMPRINT",EDGE,{"derivedFrom":subQ0}),-1.0]])]});}
            var Q22;
            {var subQ0=sQuery(id+"F0.wireOp",EDGE,"E6.58.0");Q22=makeQuery(id+"F0.imprint","IMPRINT",FACE,{"disambiguationData":[TD([[makeQuery(id+"F0.imprint","IMPRINT",EDGE,{"derivedFrom":subQ0}),-1.0]])]});}
            var Q23;
            {var subQ0=sQuery(id+"F0.wireOp",EDGE,"E6.24.0");Q23=makeQuery(id+"F0.imprint","IMPRINT",FACE,{"disambiguationData":[TD([[makeQuery(id+"F0.imprint","IMPRINT",EDGE,{"derivedFrom":subQ0}),-1.0]])]});}
            var Q24;
            {var subQ0=sQuery(id+"F0.wireOp",EDGE,"E6.40.0");Q24=makeQuery(id+"F0.imprint","IMPRINT",FACE,{"disambiguationData":[TD([[makeQuery(id+"F0.imprint","IMPRINT",EDGE,{"derivedFrom":subQ0}),-1.0]])]});}
            var Q25;
            {var subQ0=sQuery(id+"F0.wireOp",EDGE,"E6.64.0");Q25=makeQuery(id+"F0.imprint","IMPRINT",FACE,{"disambiguationData":[TD([[makeQuery(id+"F0.imprint","IMPRINT",EDGE,{"derivedFrom":subQ0}),-1.0]])]});}
            var Q26;
            {var subQ0=sQuery(id+"F0.wireOp",EDGE,"E6.66.0");Q26=makeQuery(id+"F0.imprint","IMPRINT",FACE,{"disambiguationData":[TD([[makeQuery(id+"F0.imprint","IMPRINT",EDGE,{"derivedFrom":subQ0}),-1.0]])]});}
            var Q27;
            {var subQ0=sQuery(id+"F0.wireOp",EDGE,"E6.57.0");Q27=makeQuery(id+"F0.imprint","IMPRINT",FACE,{"disambiguationData":[TD([[makeQuery(id+"F0.imprint","IMPRINT",EDGE,{"derivedFrom":subQ0}),-1.0]])]});}
            var Q28;
            {var subQ0=sQuery(id+"F0.wireOp",EDGE,"E6.63.0");Q28=makeQuery(id+"F0.imprint","IMPRINT",FACE,{"disambiguationData":[TD([[makeQuery(id+"F0.imprint","IMPRINT",EDGE,{"derivedFrom":subQ0}),-1.0]])]});}
            var Q29;
            {var subQ0=sQuery(id+"F0.wireOp",EDGE,"E6.62.0");Q29=makeQuery(id+"F0.imprint","IMPRINT",FACE,{"disambiguationData":[TD([[makeQuery(id+"F0.imprint","IMPRINT",EDGE,{"derivedFrom":subQ0}),-1.0]])]});}
            var Q30;
            {var subQ0=sQuery(id+"F0.wireOp",EDGE,"E6.60.0");Q30=makeQuery(id+"F0.imprint","IMPRINT",FACE,{"disambiguationData":[TD([[makeQuery(id+"F0.imprint","IMPRINT",EDGE,{"derivedFrom":subQ0}),-1.0]])]});}
            var Q31;
            {var subQ0=sQuery(id+"F0.wireOp",EDGE,"E6.59.0");Q31=makeQuery(id+"F0.imprint","IMPRINT",FACE,{"disambiguationData":[TD([[makeQuery(id+"F0.imprint","IMPRINT",EDGE,{"derivedFrom":subQ0}),-1.0]])]});}
            var Q32;
            {var subQ0=sQuery(id+"F0.wireOp",EDGE,"E6.8.0");Q32=makeQuery(id+"F0.imprint","IMPRINT",FACE,{"disambiguationData":[TD([[makeQuery(id+"F0.imprint","IMPRINT",EDGE,{"derivedFrom":subQ0}),-1.0]])]});}
            var Q33;
            {var subQ0=sQuery(id+"F0.wireOp",EDGE,"E6.7.0");Q33=makeQuery(id+"F0.imprint","IMPRINT",FACE,{"disambiguationData":[TD([[makeQuery(id+"F0.imprint","IMPRINT",EDGE,{"derivedFrom":subQ0}),-1.0]])]});}
            var Q34;
            {var subQ0=sQuery(id+"F0.wireOp",EDGE,"E6.23.0");Q34=makeQuery(id+"F0.imprint","IMPRINT",FACE,{"disambiguationData":[TD([[makeQuery(id+"F0.imprint","IMPRINT",EDGE,{"derivedFrom":subQ0}),-1.0]])]});}
            var Q35;
            {var subQ0=sQuery(id+"F0.wireOp",EDGE,"E6.42.0");Q35=makeQuery(id+"F0.imprint","IMPRINT",FACE,{"disambiguationData":[TD([[makeQuery(id+"F0.imprint","IMPRINT",EDGE,{"derivedFrom":subQ0}),-1.0]])]});}
            var Q36;
            {var subQ0=sQuery(id+"F0.wireOp",EDGE,"E6.11.0");Q36=makeQuery(id+"F0.imprint","IMPRINT",FACE,{"disambiguationData":[TD([[makeQuery(id+"F0.imprint","IMPRINT",EDGE,{"derivedFrom":subQ0}),-1.0]])]});}
            var Q37;
            {var subQ0=sQuery(id+"F0.wireOp",EDGE,"E6.43.0");Q37=makeQuery(id+"F0.imprint","IMPRINT",FACE,{"disambiguationData":[TD([[makeQuery(id+"F0.imprint","IMPRINT",EDGE,{"derivedFrom":subQ0}),-1.0]])]});}
            var Q38;
            {var subQ0=sQuery(id+"F0.wireOp",EDGE,"E6.10.0");Q38=makeQuery(id+"F0.imprint","IMPRINT",FACE,{"disambiguationData":[TD([[makeQuery(id+"F0.imprint","IMPRINT",EDGE,{"derivedFrom":subQ0}),-1.0]])]});}
            var Q39;
            {var subQ0=sQuery(id+"F0.wireOp",EDGE,"E6.12.0");Q39=makeQuery(id+"F0.imprint","IMPRINT",FACE,{"disambiguationData":[TD([[makeQuery(id+"F0.imprint","IMPRINT",EDGE,{"derivedFrom":subQ0}),-1.0]])]});}
            var Q40;
            {var subQ0=sQuery(id+"F0.wireOp",EDGE,"E6.28.0");Q40=makeQuery(id+"F0.imprint","IMPRINT",FACE,{"disambiguationData":[TD([[makeQuery(id+"F0.imprint","IMPRINT",EDGE,{"derivedFrom":subQ0}),-1.0]])]});}
            var Q41;
            {var subQ0=sQuery(id+"F0.wireOp",EDGE,"E6.26.0");Q41=makeQuery(id+"F0.imprint","IMPRINT",FACE,{"disambiguationData":[TD([[makeQuery(id+"F0.imprint","IMPRINT",EDGE,{"derivedFrom":subQ0}),-1.0]])]});}
            var Q42;
            {var subQ0=sQuery(id+"F0.wireOp",EDGE,"E6.44.0");Q42=makeQuery(id+"F0.imprint","IMPRINT",FACE,{"disambiguationData":[TD([[makeQuery(id+"F0.imprint","IMPRINT",EDGE,{"derivedFrom":subQ0}),-1.0]])]});}
            var Q43;
            {var subQ0=sQuery(id+"F0.wireOp",EDGE,"E6.48.0");Q43=makeQuery(id+"F0.imprint","IMPRINT",FACE,{"disambiguationData":[TD([[makeQuery(id+"F0.imprint","IMPRINT",EDGE,{"derivedFrom":subQ0}),-1.0]])]});}
            var Q44;
            {var subQ0=sQuery(id+"F0.wireOp",EDGE,"E6.69.0");Q44=makeQuery(id+"F0.imprint","IMPRINT",FACE,{"disambiguationData":[TD([[makeQuery(id+"F0.imprint","IMPRINT",EDGE,{"derivedFrom":subQ0}),-1.0]])]});}
            var Q45;
            {var subQ0=sQuery(id+"F0.wireOp",EDGE,"E6.45.0");Q45=makeQuery(id+"F0.imprint","IMPRINT",FACE,{"disambiguationData":[TD([[makeQuery(id+"F0.imprint","IMPRINT",EDGE,{"derivedFrom":subQ0}),-1.0]])]});}
            var Q46;
            {var subQ0=sQuery(id+"F0.wireOp",EDGE,"E6.31.0");Q46=makeQuery(id+"F0.imprint","IMPRINT",FACE,{"disambiguationData":[TD([[makeQuery(id+"F0.imprint","IMPRINT",EDGE,{"derivedFrom":subQ0}),-1.0]])]});}
            var Q47;
            {var subQ0=sQuery(id+"F0.wireOp",EDGE,"E6.49.0");Q47=makeQuery(id+"F0.imprint","IMPRINT",FACE,{"disambiguationData":[TD([[makeQuery(id+"F0.imprint","IMPRINT",EDGE,{"derivedFrom":subQ0}),-1.0]])]});}
            var Q48;
            {var subQ0=sQuery(id+"F0.wireOp",EDGE,"E6.1.0");Q48=makeQuery(id+"F0.imprint","IMPRINT",FACE,{"disambiguationData":[TD([[makeQuery(id+"F0.imprint","IMPRINT",EDGE,{"derivedFrom":subQ0}),-1.0]])]});}
            var Q49;
            {var subQ0=sQuery(id+"F0.wireOp",EDGE,"E6.19.0");Q49=makeQuery(id+"F0.imprint","IMPRINT",FACE,{"disambiguationData":[TD([[makeQuery(id+"F0.imprint","IMPRINT",EDGE,{"derivedFrom":subQ0}),-1.0]])]});}
            var Q50;
            {var subQ0=sQuery(id+"F0.wireOp",EDGE,"E6.3.0");Q50=makeQuery(id+"F0.imprint","IMPRINT",FACE,{"disambiguationData":[TD([[makeQuery(id+"F0.imprint","IMPRINT",EDGE,{"derivedFrom":subQ0}),-1.0]])]});}
            var Q51;
            {var subQ0=sQuery(id+"F0.wireOp",EDGE,"E6.68.0");Q51=makeQuery(id+"F0.imprint","IMPRINT",FACE,{"disambiguationData":[TD([[makeQuery(id+"F0.imprint","IMPRINT",EDGE,{"derivedFrom":subQ0}),-1.0]])]});}
            var Q52;
            {var subQ0=sQuery(id+"F0.wireOp",EDGE,"E6.55.0");Q52=makeQuery(id+"F0.imprint","IMPRINT",FACE,{"disambiguationData":[TD([[makeQuery(id+"F0.imprint","IMPRINT",EDGE,{"derivedFrom":subQ0}),-1.0]])]});}
            var Q53;
            {var subQ0=sQuery(id+"F0.wireOp",EDGE,"E6.39.0");Q53=makeQuery(id+"F0.imprint","IMPRINT",FACE,{"disambiguationData":[TD([[makeQuery(id+"F0.imprint","IMPRINT",EDGE,{"derivedFrom":subQ0}),-1.0]])]});}
            var Q54;
            {var subQ0=sQuery(id+"F0.wireOp",EDGE,"E6.67.0");Q54=makeQuery(id+"F0.imprint","IMPRINT",FACE,{"disambiguationData":[TD([[makeQuery(id+"F0.imprint","IMPRINT",EDGE,{"derivedFrom":subQ0}),-1.0]])]});}
            var Q55;
            {var subQ0=sQuery(id+"F0.wireOp",EDGE,"E6.27.0");Q55=makeQuery(id+"F0.imprint","IMPRINT",FACE,{"disambiguationData":[TD([[makeQuery(id+"F0.imprint","IMPRINT",EDGE,{"derivedFrom":subQ0}),-1.0]])]});}
            var Q56;
            {var subQ0=sQuery(id+"F0.wireOp",EDGE,"E6.17.0");Q56=makeQuery(id+"F0.imprint","IMPRINT",FACE,{"disambiguationData":[TD([[makeQuery(id+"F0.imprint","IMPRINT",EDGE,{"derivedFrom":subQ0}),-1.0]])]});}
            var Q57;
            {var subQ0=sQuery(id+"F0.wireOp",EDGE,"E6.2.0");Q57=makeQuery(id+"F0.imprint","IMPRINT",FACE,{"disambiguationData":[TD([[makeQuery(id+"F0.imprint","IMPRINT",EDGE,{"derivedFrom":subQ0}),-1.0]])]});}
            var Q58;
            {var subQ0=sQuery(id+"F0.wireOp",EDGE,"E1");Q58=makeQuery(id+"F0.imprint","IMPRINT",FACE,{"disambiguationData":[TD([[makeQuery(id+"F0.imprint","IMPRINT",EDGE,{"derivedFrom":subQ0}),1.0]])]});}
            var Q59;
            {var subQ0=sQuery(id+"F0.wireOp",EDGE,"E1");Q59=makeQuery(id+"F0.imprint","IMPRINT",FACE,{"disambiguationData":[TD([[makeQuery(id+"F0.imprint","IMPRINT",EDGE,{"derivedFrom":subQ0}),-1.0]])]});}
            var Q60;
            {var subQ0=sQuery(id+"F0.wireOp",EDGE,"E0");var subQ69=makeQuery(id+"F0.imprint","INTERSECT",VERTEX,{"derivedFrom":[subQ0,sQuery(id+"F0.wireOp",EDGE,"E6.53.0")]});Q60=makeQuery(id+"F0.imprint","IMPRINT",FACE,{"disambiguationData":[TD([[makeQuery(id+"F0.imprint","IMPRINT",EDGE,{"disambiguationData":[TD([[subQ69,-1.0]])],"derivedFrom":subQ0}),1.0]])]});}
            var Q61;
            {var subQ0=sQuery(id+"F0.wireOp",EDGE,"E6.54.0");Q61=makeQuery(id+"F0.imprint","IMPRINT",FACE,{"disambiguationData":[TD([[makeQuery(id+"F0.imprint","IMPRINT",EDGE,{"derivedFrom":subQ0}),-1.0]])]});}
            var Q62;
            {var subQ0=sQuery(id+"F0.wireOp",EDGE,"E6.32.0");Q62=makeQuery(id+"F0.imprint","IMPRINT",FACE,{"disambiguationData":[TD([[makeQuery(id+"F0.imprint","IMPRINT",EDGE,{"derivedFrom":subQ0}),-1.0]])]});}
            var Q63;
            {var subQ0=sQuery(id+"F0.wireOp",EDGE,"E6.51.0");Q63=makeQuery(id+"F0.imprint","IMPRINT",FACE,{"disambiguationData":[TD([[makeQuery(id+"F0.imprint","IMPRINT",EDGE,{"derivedFrom":subQ0}),-1.0]])]});}
            var Q64;
            {var subQ0=sQuery(id+"F0.wireOp",EDGE,"E6.34.0");Q64=makeQuery(id+"F0.imprint","IMPRINT",FACE,{"disambiguationData":[TD([[makeQuery(id+"F0.imprint","IMPRINT",EDGE,{"derivedFrom":subQ0}),-1.0]])]});}
            var Q65;
            {var subQ0=sQuery(id+"F0.wireOp",EDGE,"E6.35.0");Q65=makeQuery(id+"F0.imprint","IMPRINT",FACE,{"disambiguationData":[TD([[makeQuery(id+"F0.imprint","IMPRINT",EDGE,{"derivedFrom":subQ0}),-1.0]])]});}
            var Q66;
            {var subQ0=sQuery(id+"F0.wireOp",EDGE,"E6.52.0");Q66=makeQuery(id+"F0.imprint","IMPRINT",FACE,{"disambiguationData":[TD([[makeQuery(id+"F0.imprint","IMPRINT",EDGE,{"derivedFrom":subQ0}),-1.0]])]});}
            var Q67;
            {var subQ0=sQuery(id+"F0.wireOp",EDGE,"E6.36.0");Q67=makeQuery(id+"F0.imprint","IMPRINT",FACE,{"disambiguationData":[TD([[makeQuery(id+"F0.imprint","IMPRINT",EDGE,{"derivedFrom":subQ0}),-1.0]])]});}
            var Q68;
            {var subQ0=sQuery(id+"F0.wireOp",EDGE,"E6.38.0");Q68=makeQuery(id+"F0.imprint","IMPRINT",FACE,{"disambiguationData":[TD([[makeQuery(id+"F0.imprint","IMPRINT",EDGE,{"derivedFrom":subQ0}),-1.0]])]});}
            var Q69;
            {var subQ0=sQuery(id+"F0.wireOp",EDGE,"E6.37.0");Q69=makeQuery(id+"F0.imprint","IMPRINT",FACE,{"disambiguationData":[TD([[makeQuery(id+"F0.imprint","IMPRINT",EDGE,{"derivedFrom":subQ0}),-1.0]])]});}
            var Q70;
            {var subQ0=sQuery(id+"F0.wireOp",EDGE,"E6.53.0");Q70=makeQuery(id+"F0.imprint","IMPRINT",FACE,{"disambiguationData":[TD([[makeQuery(id+"F0.imprint","IMPRINT",EDGE,{"derivedFrom":subQ0}),-1.0]])]});}
            var Q71;
            {var subQ0=sQuery(id+"F0.wireOp",EDGE,"E6.33.0");Q71=makeQuery(id+"F0.imprint","IMPRINT",FACE,{"disambiguationData":[TD([[makeQuery(id+"F0.imprint","IMPRINT",EDGE,{"derivedFrom":subQ0}),-1.0]])]});}
            extrude(context, id + "F1", {"entities" : qUnion([Q0, Q1, Q2, Q3, Q4, Q5, Q6, Q7, Q8, Q9, Q10, Q11, Q12, Q13, Q14, Q15, Q16, Q17, Q18, Q19, Q20, Q21, Q22, Q23, Q24, Q25, Q26, Q27, Q28, Q29, Q30, Q31, Q32, Q33, Q34, Q35, Q36, Q37, Q38, Q39, Q40, Q41, Q42, Q43, Q44, Q45, Q46, Q47, Q48, Q49, Q50, Q51, Q52, Q53, Q54, Q55, Q56, Q57, Q58, Q59, Q60, Q61, Q62, Q63, Q64, Q65, Q66, Q67, Q68, Q69, Q70, Q71]), "depth" : 6.35 * mm});
        }
        {
            var Q0;
            Q0=makeQuery(id+"F1.opExtrude","CAP_FACE",FACE,{"disambiguationData":[OSD([sQuery(id+"F0.wireOp",EDGE,"E0"),sQuery(id+"F0.wireOp",EDGE,"E2"),sQuery(id+"F0.wireOp",EDGE,"E3"),sQuery(id+"F0.wireOp",EDGE,"E4"),sQuery(id+"F0.wireOp",EDGE,"E5"),sQuery(id+"F0.wireOp",EDGE,"E6.1.0"),sQuery(id+"F0.wireOp",EDGE,"E6.1.1"),sQuery(id+"F0.wireOp",EDGE,"E6.1.2"),sQuery(id+"F0.wireOp",EDGE,"E6.1.3"),sQuery(id+"F0.wireOp",EDGE,"E6.2.0"),sQuery(id+"F0.wireOp",EDGE,"E6.2.1"),sQuery(id+"F0.wireOp",EDGE,"E6.2.2"),sQuery(id+"F0.wireOp",EDGE,"E6.2.3"),sQuery(id+"F0.wireOp",EDGE,"E6.3.0"),sQuery(id+"F0.wireOp",EDGE,"E6.3.1"),sQuery(id+"F0.wireOp",EDGE,"E6.3.2"),sQuery(id+"F0.wireOp",EDGE,"E6.3.3"),sQuery(id+"F0.wireOp",EDGE,"E6.4.0"),sQuery(id+"F0.wireOp",EDGE,"E6.4.1"),sQuery(id+"F0.wireOp",EDGE,"E6.4.2"),sQuery(id+"F0.wireOp",EDGE,"E6.4.3"),sQuery(id+"F0.wireOp",EDGE,"E6.5.0"),sQuery(id+"F0.wireOp",EDGE,"E6.5.1"),sQuery(id+"F0.wireOp",EDGE,"E6.5.2"),sQuery(id+"F0.wireOp",EDGE,"E6.5.3"),sQuery(id+"F0.wireOp",EDGE,"E6.6.0"),sQuery(id+"F0.wireOp",EDGE,"E6.6.1"),sQuery(id+"F0.wireOp",EDGE,"E6.6.2"),sQuery(id+"F0.wireOp",EDGE,"E6.6.3"),sQuery(id+"F0.wireOp",EDGE,"E6.7.0"),sQuery(id+"F0.wireOp",EDGE,"E6.7.1"),sQuery(id+"F0.wireOp",EDGE,"E6.7.2"),sQuery(id+"F0.wireOp",EDGE,"E6.7.3"),sQuery(id+"F0.wireOp",EDGE,"E6.8.0"),sQuery(id+"F0.wireOp",EDGE,"E6.8.1"),sQuery(id+"F0.wireOp",EDGE,"E6.8.2"),sQuery(id+"F0.wireOp",EDGE,"E6.8.3"),sQuery(id+"F0.wireOp",EDGE,"E6.9.0"),sQuery(id+"F0.wireOp",EDGE,"E6.9.1"),sQuery(id+"F0.wireOp",EDGE,"E6.9.2"),sQuery(id+"F0.wireOp",EDGE,"E6.9.3"),sQuery(id+"F0.wireOp",EDGE,"E6.10.0"),sQuery(id+"F0.wireOp",EDGE,"E6.10.1"),sQuery(id+"F0.wireOp",EDGE,"E6.10.2"),sQuery(id+"F0.wireOp",EDGE,"E6.10.3"),sQuery(id+"F0.wireOp",EDGE,"E6.11.0"),sQuery(id+"F0.wireOp",EDGE,"E6.11.1"),sQuery(id+"F0.wireOp",EDGE,"E6.11.2"),sQuery(id+"F0.wireOp",EDGE,"E6.11.3"),sQuery(id+"F0.wireOp",EDGE,"E6.12.0"),sQuery(id+"F0.wireOp",EDGE,"E6.12.1"),sQuery(id+"F0.wireOp",EDGE,"E6.12.2"),sQuery(id+"F0.wireOp",EDGE,"E6.12.3"),sQuery(id+"F0.wireOp",EDGE,"E6.13.0"),sQuery(id+"F0.wireOp",EDGE,"E6.13.1"),sQuery(id+"F0.wireOp",EDGE,"E6.13.2"),sQuery(id+"F0.wireOp",EDGE,"E6.13.3"),sQuery(id+"F0.wireOp",EDGE,"E6.14.0"),sQuery(id+"F0.wireOp",EDGE,"E6.14.1"),sQuery(id+"F0.wireOp",EDGE,"E6.14.2"),sQuery(id+"F0.wireOp",EDGE,"E6.14.3"),sQuery(id+"F0.wireOp",EDGE,"E6.15.0"),sQuery(id+"F0.wireOp",EDGE,"E6.15.1"),sQuery(id+"F0.wireOp",EDGE,"E6.15.2"),sQuery(id+"F0.wireOp",EDGE,"E6.15.3"),sQuery(id+"F0.wireOp",EDGE,"E6.16.0"),sQuery(id+"F0.wireOp",EDGE,"E6.16.1"),sQuery(id+"F0.wireOp",EDGE,"E6.16.2"),sQuery(id+"F0.wireOp",EDGE,"E6.16.3"),sQuery(id+"F0.wireOp",EDGE,"E6.17.0"),sQuery(id+"F0.wireOp",EDGE,"E6.17.1"),sQuery(id+"F0.wireOp",EDGE,"E6.17.2"),sQuery(id+"F0.wireOp",EDGE,"E6.17.3"),sQuery(id+"F0.wireOp",EDGE,"E6.18.0"),sQuery(id+"F0.wireOp",EDGE,"E6.18.1"),sQuery(id+"F0.wireOp",EDGE,"E6.18.2"),sQuery(id+"F0.wireOp",EDGE,"E6.18.3"),sQuery(id+"F0.wireOp",EDGE,"E6.19.0"),sQuery(id+"F0.wireOp",EDGE,"E6.19.1"),sQuery(id+"F0.wireOp",EDGE,"E6.19.2"),sQuery(id+"F0.wireOp",EDGE,"E6.19.3"),sQuery(id+"F0.wireOp",EDGE,"E6.20.0"),sQuery(id+"F0.wireOp",EDGE,"E6.20.1"),sQuery(id+"F0.wireOp",EDGE,"E6.20.2"),sQuery(id+"F0.wireOp",EDGE,"E6.20.3"),sQuery(id+"F0.wireOp",EDGE,"E6.21.0"),sQuery(id+"F0.wireOp",EDGE,"E6.21.1"),sQuery(id+"F0.wireOp",EDGE,"E6.21.2"),sQuery(id+"F0.wireOp",EDGE,"E6.21.3"),sQuery(id+"F0.wireOp",EDGE,"E6.22.0"),sQuery(id+"F0.wireOp",EDGE,"E6.22.1"),sQuery(id+"F0.wireOp",EDGE,"E6.22.2"),sQuery(id+"F0.wireOp",EDGE,"E6.22.3"),sQuery(id+"F0.wireOp",EDGE,"E6.23.0"),sQuery(id+"F0.wireOp",EDGE,"E6.23.1"),sQuery(id+"F0.wireOp",EDGE,"E6.23.2"),sQuery(id+"F0.wireOp",EDGE,"E6.23.3"),sQuery(id+"F0.wireOp",EDGE,"E6.24.0"),sQuery(id+"F0.wireOp",EDGE,"E6.24.1"),sQuery(id+"F0.wireOp",EDGE,"E6.24.2"),sQuery(id+"F0.wireOp",EDGE,"E6.24.3"),sQuery(id+"F0.wireOp",EDGE,"E6.25.0"),sQuery(id+"F0.wireOp",EDGE,"E6.25.1"),sQuery(id+"F0.wireOp",EDGE,"E6.25.2"),sQuery(id+"F0.wireOp",EDGE,"E6.25.3"),sQuery(id+"F0.wireOp",EDGE,"E6.26.0"),sQuery(id+"F0.wireOp",EDGE,"E6.26.1"),sQuery(id+"F0.wireOp",EDGE,"E6.26.2"),sQuery(id+"F0.wireOp",EDGE,"E6.26.3"),sQuery(id+"F0.wireOp",EDGE,"E6.27.0"),sQuery(id+"F0.wireOp",EDGE,"E6.27.1"),sQuery(id+"F0.wireOp",EDGE,"E6.27.2"),sQuery(id+"F0.wireOp",EDGE,"E6.27.3"),sQuery(id+"F0.wireOp",EDGE,"E6.28.0"),sQuery(id+"F0.wireOp",EDGE,"E6.28.1"),sQuery(id+"F0.wireOp",EDGE,"E6.28.2"),sQuery(id+"F0.wireOp",EDGE,"E6.28.3"),sQuery(id+"F0.wireOp",EDGE,"E6.29.0"),sQuery(id+"F0.wireOp",EDGE,"E6.29.1"),sQuery(id+"F0.wireOp",EDGE,"E6.29.2"),sQuery(id+"F0.wireOp",EDGE,"E6.29.3"),sQuery(id+"F0.wireOp",EDGE,"E6.30.0"),sQuery(id+"F0.wireOp",EDGE,"E6.30.1"),sQuery(id+"F0.wireOp",EDGE,"E6.30.2"),sQuery(id+"F0.wireOp",EDGE,"E6.30.3"),sQuery(id+"F0.wireOp",EDGE,"E6.31.0"),sQuery(id+"F0.wireOp",EDGE,"E6.31.1"),sQuery(id+"F0.wireOp",EDGE,"E6.31.2"),sQuery(id+"F0.wireOp",EDGE,"E6.31.3"),sQuery(id+"F0.wireOp",EDGE,"E6.32.0"),sQuery(id+"F0.wireOp",EDGE,"E6.32.1"),sQuery(id+"F0.wireOp",EDGE,"E6.32.2"),sQuery(id+"F0.wireOp",EDGE,"E6.32.3"),sQuery(id+"F0.wireOp",EDGE,"E6.33.0"),sQuery(id+"F0.wireOp",EDGE,"E6.33.1"),sQuery(id+"F0.wireOp",EDGE,"E6.33.2"),sQuery(id+"F0.wireOp",EDGE,"E6.33.3"),sQuery(id+"F0.wireOp",EDGE,"E6.34.0"),sQuery(id+"F0.wireOp",EDGE,"E6.34.1"),sQuery(id+"F0.wireOp",EDGE,"E6.34.2"),sQuery(id+"F0.wireOp",EDGE,"E6.34.3"),sQuery(id+"F0.wireOp",EDGE,"E6.35.0"),sQuery(id+"F0.wireOp",EDGE,"E6.35.1"),sQuery(id+"F0.wireOp",EDGE,"E6.35.2"),sQuery(id+"F0.wireOp",EDGE,"E6.35.3"),sQuery(id+"F0.wireOp",EDGE,"E6.36.0"),sQuery(id+"F0.wireOp",EDGE,"E6.36.1"),sQuery(id+"F0.wireOp",EDGE,"E6.36.2"),sQuery(id+"F0.wireOp",EDGE,"E6.36.3"),sQuery(id+"F0.wireOp",EDGE,"E6.37.0"),sQuery(id+"F0.wireOp",EDGE,"E6.37.1"),sQuery(id+"F0.wireOp",EDGE,"E6.37.2"),sQuery(id+"F0.wireOp",EDGE,"E6.37.3"),sQuery(id+"F0.wireOp",EDGE,"E6.38.0"),sQuery(id+"F0.wireOp",EDGE,"E6.38.1"),sQuery(id+"F0.wireOp",EDGE,"E6.38.2"),sQuery(id+"F0.wireOp",EDGE,"E6.38.3"),sQuery(id+"F0.wireOp",EDGE,"E6.39.0"),sQuery(id+"F0.wireOp",EDGE,"E6.39.1"),sQuery(id+"F0.wireOp",EDGE,"E6.39.2"),sQuery(id+"F0.wireOp",EDGE,"E6.39.3"),sQuery(id+"F0.wireOp",EDGE,"E6.40.0"),sQuery(id+"F0.wireOp",EDGE,"E6.40.1"),sQuery(id+"F0.wireOp",EDGE,"E6.40.2"),sQuery(id+"F0.wireOp",EDGE,"E6.40.3"),sQuery(id+"F0.wireOp",EDGE,"E6.41.0"),sQuery(id+"F0.wireOp",EDGE,"E6.41.1"),sQuery(id+"F0.wireOp",EDGE,"E6.41.2"),sQuery(id+"F0.wireOp",EDGE,"E6.41.3"),sQuery(id+"F0.wireOp",EDGE,"E6.42.0"),sQuery(id+"F0.wireOp",EDGE,"E6.42.1"),sQuery(id+"F0.wireOp",EDGE,"E6.42.2"),sQuery(id+"F0.wireOp",EDGE,"E6.42.3"),sQuery(id+"F0.wireOp",EDGE,"E6.43.0"),sQuery(id+"F0.wireOp",EDGE,"E6.43.1"),sQuery(id+"F0.wireOp",EDGE,"E6.43.2"),sQuery(id+"F0.wireOp",EDGE,"E6.43.3"),sQuery(id+"F0.wireOp",EDGE,"E6.44.0"),sQuery(id+"F0.wireOp",EDGE,"E6.44.1"),sQuery(id+"F0.wireOp",EDGE,"E6.44.2"),sQuery(id+"F0.wireOp",EDGE,"E6.44.3"),sQuery(id+"F0.wireOp",EDGE,"E6.45.0"),sQuery(id+"F0.wireOp",EDGE,"E6.45.1"),sQuery(id+"F0.wireOp",EDGE,"E6.45.2"),sQuery(id+"F0.wireOp",EDGE,"E6.45.3"),sQuery(id+"F0.wireOp",EDGE,"E6.46.0"),sQuery(id+"F0.wireOp",EDGE,"E6.46.1"),sQuery(id+"F0.wireOp",EDGE,"E6.46.2"),sQuery(id+"F0.wireOp",EDGE,"E6.46.3"),sQuery(id+"F0.wireOp",EDGE,"E6.47.0"),sQuery(id+"F0.wireOp",EDGE,"E6.47.1"),sQuery(id+"F0.wireOp",EDGE,"E6.47.2"),sQuery(id+"F0.wireOp",EDGE,"E6.47.3"),sQuery(id+"F0.wireOp",EDGE,"E6.48.0"),sQuery(id+"F0.wireOp",EDGE,"E6.48.1"),sQuery(id+"F0.wireOp",EDGE,"E6.48.2"),sQuery(id+"F0.wireOp",EDGE,"E6.48.3"),sQuery(id+"F0.wireOp",EDGE,"E6.49.0"),sQuery(id+"F0.wireOp",EDGE,"E6.49.1"),sQuery(id+"F0.wireOp",EDGE,"E6.49.2"),sQuery(id+"F0.wireOp",EDGE,"E6.49.3"),sQuery(id+"F0.wireOp",EDGE,"E6.50.0"),sQuery(id+"F0.wireOp",EDGE,"E6.50.1"),sQuery(id+"F0.wireOp",EDGE,"E6.50.2"),sQuery(id+"F0.wireOp",EDGE,"E6.50.3"),sQuery(id+"F0.wireOp",EDGE,"E6.51.0"),sQuery(id+"F0.wireOp",EDGE,"E6.51.1"),sQuery(id+"F0.wireOp",EDGE,"E6.51.2"),sQuery(id+"F0.wireOp",EDGE,"E6.51.3"),sQuery(id+"F0.wireOp",EDGE,"E6.52.0"),sQuery(id+"F0.wireOp",EDGE,"E6.52.1"),sQuery(id+"F0.wireOp",EDGE,"E6.52.2"),sQuery(id+"F0.wireOp",EDGE,"E6.52.3"),sQuery(id+"F0.wireOp",EDGE,"E6.53.0"),sQuery(id+"F0.wireOp",EDGE,"E6.53.1"),sQuery(id+"F0.wireOp",EDGE,"E6.53.2"),sQuery(id+"F0.wireOp",EDGE,"E6.53.3"),sQuery(id+"F0.wireOp",EDGE,"E6.54.0"),sQuery(id+"F0.wireOp",EDGE,"E6.54.1"),sQuery(id+"F0.wireOp",EDGE,"E6.54.2"),sQuery(id+"F0.wireOp",EDGE,"E6.54.3"),sQuery(id+"F0.wireOp",EDGE,"E6.55.0"),sQuery(id+"F0.wireOp",EDGE,"E6.55.1"),sQuery(id+"F0.wireOp",EDGE,"E6.55.2"),sQuery(id+"F0.wireOp",EDGE,"E6.55.3"),sQuery(id+"F0.wireOp",EDGE,"E6.56.0"),sQuery(id+"F0.wireOp",EDGE,"E6.56.1"),sQuery(id+"F0.wireOp",EDGE,"E6.56.2"),sQuery(id+"F0.wireOp",EDGE,"E6.56.3"),sQuery(id+"F0.wireOp",EDGE,"E6.57.0"),sQuery(id+"F0.wireOp",EDGE,"E6.57.1"),sQuery(id+"F0.wireOp",EDGE,"E6.57.2"),sQuery(id+"F0.wireOp",EDGE,"E6.57.3"),sQuery(id+"F0.wireOp",EDGE,"E6.58.0"),sQuery(id+"F0.wireOp",EDGE,"E6.58.1"),sQuery(id+"F0.wireOp",EDGE,"E6.58.2"),sQuery(id+"F0.wireOp",EDGE,"E6.58.3"),sQuery(id+"F0.wireOp",EDGE,"E6.59.0"),sQuery(id+"F0.wireOp",EDGE,"E6.59.1"),sQuery(id+"F0.wireOp",EDGE,"E6.59.2"),sQuery(id+"F0.wireOp",EDGE,"E6.59.3"),sQuery(id+"F0.wireOp",EDGE,"E6.60.0"),sQuery(id+"F0.wireOp",EDGE,"E6.60.1"),sQuery(id+"F0.wireOp",EDGE,"E6.60.2"),sQuery(id+"F0.wireOp",EDGE,"E6.60.3"),sQuery(id+"F0.wireOp",EDGE,"E6.61.0"),sQuery(id+"F0.wireOp",EDGE,"E6.61.1"),sQuery(id+"F0.wireOp",EDGE,"E6.61.2"),sQuery(id+"F0.wireOp",EDGE,"E6.61.3"),sQuery(id+"F0.wireOp",EDGE,"E6.62.0"),sQuery(id+"F0.wireOp",EDGE,"E6.62.1"),sQuery(id+"F0.wireOp",EDGE,"E6.62.2"),sQuery(id+"F0.wireOp",EDGE,"E6.62.3"),sQuery(id+"F0.wireOp",EDGE,"E6.63.0"),sQuery(id+"F0.wireOp",EDGE,"E6.63.1"),sQuery(id+"F0.wireOp",EDGE,"E6.63.2"),sQuery(id+"F0.wireOp",EDGE,"E6.63.3"),sQuery(id+"F0.wireOp",EDGE,"E6.64.0"),sQuery(id+"F0.wireOp",EDGE,"E6.64.1"),sQuery(id+"F0.wireOp",EDGE,"E6.64.2"),sQuery(id+"F0.wireOp",EDGE,"E6.64.3"),sQuery(id+"F0.wireOp",EDGE,"E6.65.0"),sQuery(id+"F0.wireOp",EDGE,"E6.65.1"),sQuery(id+"F0.wireOp",EDGE,"E6.65.2"),sQuery(id+"F0.wireOp",EDGE,"E6.65.3"),sQuery(id+"F0.wireOp",EDGE,"E6.66.0"),sQuery(id+"F0.wireOp",EDGE,"E6.66.1"),sQuery(id+"F0.wireOp",EDGE,"E6.66.2"),sQuery(id+"F0.wireOp",EDGE,"E6.66.3"),sQuery(id+"F0.wireOp",EDGE,"E6.67.0"),sQuery(id+"F0.wireOp",EDGE,"E6.67.1"),sQuery(id+"F0.wireOp",EDGE,"E6.67.2"),sQuery(id+"F0.wireOp",EDGE,"E6.67.3"),sQuery(id+"F0.wireOp",EDGE,"E6.68.0"),sQuery(id+"F0.wireOp",EDGE,"E6.68.1"),sQuery(id+"F0.wireOp",EDGE,"E6.68.2"),sQuery(id+"F0.wireOp",EDGE,"E6.68.3"),sQuery(id+"F0.wireOp",EDGE,"E6.69.0"),sQuery(id+"F0.wireOp",EDGE,"E6.69.1"),sQuery(id+"F0.wireOp",EDGE,"E6.69.2"),sQuery(id+"F0.wireOp",EDGE,"E6.69.3")])],"isStart":false});
            var sketch = newSketch(context, id + "F2", { "sketchPlane" : qUnion([Q0])});
            skCircle(sketch, "E7", {"center": v(0, 0) * mm, "radius": 1.27 * mm});
            skSolve(sketch);
        }
        {
            var Q0;
            Q0=makeQuery(id+"F2.imprint","IMPRINT",FACE,{"disambiguationData":[TD([[makeQuery(id+"F2.imprint","IMPRINT",EDGE,{"derivedFrom":sQuery(id+"F2.wireOp",EDGE,"E7")}),1.0]])]});
            extrude(context, id + "F3", {"entities" : qUnion([Q0]), "operationType" : NewBodyOperationType.REMOVE, "oppositeDirection" : true, "depth" : 6.35 * mm});
        }
    });
